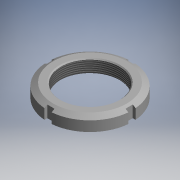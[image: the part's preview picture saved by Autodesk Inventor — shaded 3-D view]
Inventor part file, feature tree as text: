
AUTODESK INVENTOR PART (.ipt)
format: ipt  version: 2017.3 (Build 213256000, 256)  size: 135,168 bytes
history: native  units: mm (DEFAULTED — no unit token found)
features: other x7, sketch x2, revolve x1, thread x1, extrude x1
ambient origin geometry x8: Origin, YZ Plane, XZ Plane, XY Plane, X Axis, Y Axis, Z Axis, Center Point
bodies: Solid1 (feature_tree)
feature tree (12):
  revolve  "Revolution1"  [1 undecoded]
  thread  "Thread1"  [1 undecoded]
  extrude  "Extrusion1"  [1 undecoded]
  other  "wash_to_nut_XY"
  other  "wash_to_nut_YZ"
  other  "wash_to_nut_ZX"
  other  "wash_to_nut_X"
  other  "wash_to_nut_Y"
  other  "wash_to_nut_Z"
  other  "wash_to_nut_Center"
  sketch  "Sketch_1"  dims[d0=360.0deg d1=9.376mm d2=0.0mm d3=11.0mm d4=0.0mm]
  sketch  "Sketch_2"  dims[d5=0.0mm]
note: 3 required parameter values undecoded (feature->parameter linkage not recoverable at this tier; creation-order binding heuristic only, values carry confidence <= 0.55)